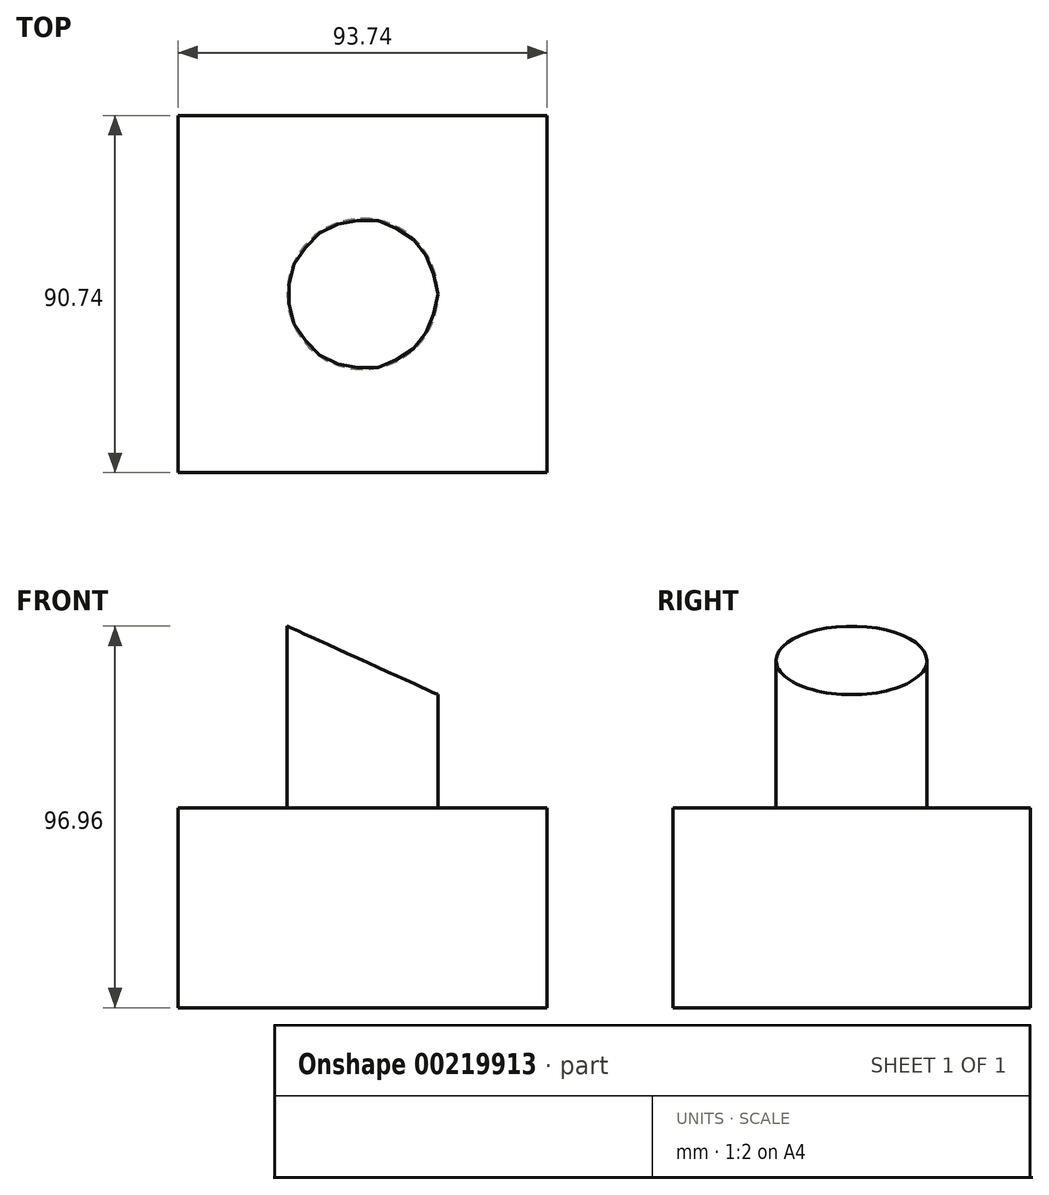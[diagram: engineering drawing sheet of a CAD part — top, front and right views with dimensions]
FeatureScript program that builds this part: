
annotation { "Feature Type Name" : "Feature", "Feature Type Description" : "" }
export const myFeature = defineFeature(function(context is Context, id is Id, definition is map)
    precondition{}
    {
        {
            var Q0;
            Q0=qCreatedBy(makeId("Top.planeOp"),FACE);
            var sketch = newSketch(context, id + "F0", { "sketchPlane" : qUnion([Q0])});
            skLineSegment(sketch, "E0.bottom", {"start": v(46.87, 45.37) * mm, "end": v(-46.87, 45.37) * mm});
            skLineSegment(sketch, "E0.top", {"start": v(46.87, -45.37) * mm, "end": v(-46.87, -45.37) * mm});
            skLineSegment(sketch, "E0.left", {"start": v(46.87, 45.37) * mm, "end": v(46.87, -45.37) * mm});
            skLineSegment(sketch, "E0.right", {"start": v(-46.87, 45.37) * mm, "end": v(-46.87, -45.37) * mm});
            skPoint(sketch, "E0.middle", {"position": v(0, 0) * mm});
            skSolve(sketch);
        }
        {
            var Q0;
            Q0 = qSketchRegion(id + "F0", true);
            extrude(context, id + "F1", {"entities" : qUnion([Q0]), "depth" : 50.8 * mm});
        }
        {
            var Q0;
            Q0=makeQuery(id+"F1.opExtrude","CAP_FACE",FACE,{"disambiguationData":[OSD([sQuery(id+"F0.wireOp",EDGE,"E0.bottom"),sQuery(id+"F0.wireOp",EDGE,"E0.top"),sQuery(id+"F0.wireOp",EDGE,"E0.left"),sQuery(id+"F0.wireOp",EDGE,"E0.right")])],"isStart":false});
            var sketch = newSketch(context, id + "F2", { "sketchPlane" : qUnion([Q0])});
            skCircle(sketch, "E1", {"center": v(0, 0) * mm, "radius": 19.19 * mm});
            skSolve(sketch);
        }
        {
            var Q0;
            Q0 = qSketchRegion(id + "F2", true);
            extrude(context, id + "F3", {"entities" : qUnion([Q0]), "operationType" : NewBodyOperationType.ADD, "depth" : 50.8 * mm});
        }
        {
            var Q0;
            Q0=qCreatedBy(makeId("Front.planeOp"),FACE);
            var sketch = newSketch(context, id + "F4", { "sketchPlane" : qUnion([Q0])});
            skLineSegment(sketch, "E2", {"start": v(-43.91, 108.2) * mm, "end": v(59.8, 108.2) * mm});
            skLineSegment(sketch, "E3", {"start": v(59.8, 108.2) * mm, "end": v(59.8, 61.06) * mm});
            skLineSegment(sketch, "E4", {"start": v(59.8, 61.06) * mm, "end": v(-43.91, 108.2) * mm});
            skSolve(sketch);
        }
        {
            var Q0;
            Q0 = qSketchRegion(id + "F4", true);
            extrude(context, id + "F5", {"entities" : qUnion([Q0]), "operationType" : NewBodyOperationType.REMOVE, "endBound" : BoundingType.SYMMETRIC, "oppositeDirection" : true, "depth" : 135.13 * mm});
        }
    });
